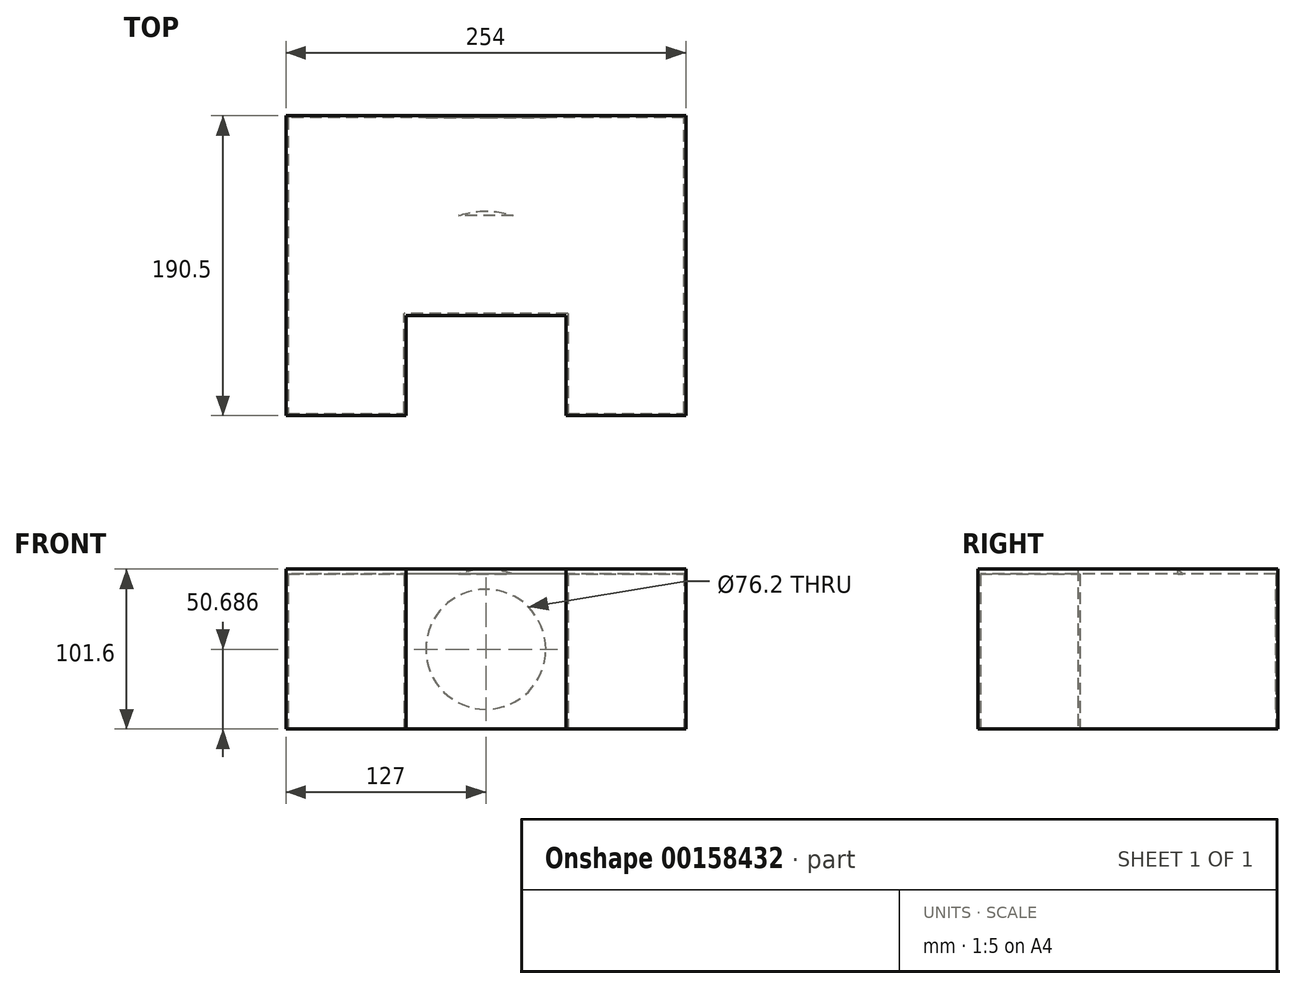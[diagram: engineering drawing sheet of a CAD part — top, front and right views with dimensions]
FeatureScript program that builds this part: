
annotation { "Feature Type Name" : "Feature", "Feature Type Description" : "" }
export const myFeature = defineFeature(function(context is Context, id is Id, definition is map)
    precondition{}
    {
        {
            var Q0;
            Q0=qCreatedBy(makeId("Top.planeOp"),FACE);
            var sketch = newSketch(context, id + "F0", { "sketchPlane" : qUnion([Q0])});
            skLineSegment(sketch, "E0.bottom", {"start": v(127, -63.5) * mm, "end": v(-127, -63.5) * mm});
            skLineSegment(sketch, "E0.top", {"start": v(127, 63.5) * mm, "end": v(-127, 63.5) * mm});
            skLineSegment(sketch, "E0.left", {"start": v(127, -63.5) * mm, "end": v(127, 63.5) * mm});
            skLineSegment(sketch, "E0.right", {"start": v(-127, -63.5) * mm, "end": v(-127, 63.5) * mm});
            skPoint(sketch, "E0.middle", {"position": v(0, 0) * mm});
            skLineSegment(sketch, "E1", {"start": v(-127, -63.5) * mm, "end": v(-50.8, -63.5) * mm});
            skLineSegment(sketch, "E2", {"start": v(127, -63.5) * mm, "end": v(50.8, -63.5) * mm});
            skLineSegment(sketch, "E3", {"start": v(-127, -63.5) * mm, "end": v(-127, -127) * mm});
            skLineSegment(sketch, "E4", {"start": v(127, -63.5) * mm, "end": v(127, -127) * mm});
            skLineSegment(sketch, "E5", {"start": v(-127, -127) * mm, "end": v(-50.8, -127) * mm});
            skLineSegment(sketch, "E6", {"start": v(127, -127) * mm, "end": v(50.8, -127) * mm});
            skLineSegment(sketch, "E7", {"start": v(-50.8, -63.5) * mm, "end": v(-50.8, -127) * mm});
            skLineSegment(sketch, "E8", {"start": v(50.8, -63.5) * mm, "end": v(50.8, -127) * mm});
            skSolve(sketch);
        }
        {
            var Q0;
            Q0 = qSketchRegion(id + "F0", true);
            extrude(context, id + "F1", {"entities" : qUnion([Q0]), "depth" : 101.6 * mm});
        }
        {
            var Q0;
            Q0=qCreatedBy(makeId("Top.planeOp"),FACE);
            var sketch = newSketch(context, id + "F2", { "sketchPlane" : qUnion([Q0])});
            skLineSegment(sketch, "E9.bottom", {"start": v(125.73, -62.23) * mm, "end": v(-125.73, -62.23) * mm});
            skLineSegment(sketch, "E9.top", {"start": v(125.73, 62.23) * mm, "end": v(-125.73, 62.23) * mm});
            skLineSegment(sketch, "E9.left", {"start": v(125.73, -62.23) * mm, "end": v(125.73, 62.23) * mm});
            skLineSegment(sketch, "E9.right", {"start": v(-125.73, -62.23) * mm, "end": v(-125.73, 62.23) * mm});
            skPoint(sketch, "E9.middle", {"position": v(0, 0) * mm});
            skLineSegment(sketch, "E10", {"start": v(-125.73, -62.23) * mm, "end": v(-125.73, -125.48) * mm});
            skLineSegment(sketch, "E11", {"start": v(-125.73, -125.48) * mm, "end": v(-52.07, -125.48) * mm});
            skLineSegment(sketch, "E12", {"start": v(-52.07, -125.48) * mm, "end": v(-52.07, -62.23) * mm});
            skLineSegment(sketch, "E13", {"start": v(-52.07, -62.23) * mm, "end": v(52.07, -62.23) * mm});
            skLineSegment(sketch, "E14", {"start": v(52.07, -62.23) * mm, "end": v(52.07, -125.48) * mm});
            skLineSegment(sketch, "E15", {"start": v(52.07, -125.48) * mm, "end": v(125.73, -125.48) * mm});
            skLineSegment(sketch, "E16", {"start": v(125.73, -125.48) * mm, "end": v(125.73, -62.23) * mm});
            skSolve(sketch);
        }
        {
            var Q0;
            Q0 = qSketchRegion(id + "F2", true);
            extrude(context, id + "F3", {"entities" : qUnion([Q0]), "operationType" : NewBodyOperationType.REMOVE, "depth" : 98.42 * mm});
        }
        {
            var Q0;
            Q0=qCreatedBy(makeId("Front.planeOp"),FACE);
            var sketch = newSketch(context, id + "F4", { "sketchPlane" : qUnion([Q0])});
            skCircle(sketch, "E17", {"center": v(0, 50.69) * mm, "radius": 50.33 * mm});
            skSolve(sketch);
        }
        {
            var Q0;
            Q0=sQuery(id+"F4.wireOp",VERTEX,"E17.center");
            var Q1;
            Q1=makeQuery(id+"F1.opExtrude","SWEPT_BODY",BODY,{"disambiguationData":[OSD([sQuery(id+"F0.wireOp",EDGE,"E0.bottom"),sQuery(id+"F0.wireOp",EDGE,"E0.top"),sQuery(id+"F0.wireOp",EDGE,"E0.left"),sQuery(id+"F0.wireOp",EDGE,"E0.right"),sQuery(id+"F0.wireOp",EDGE,"E3"),sQuery(id+"F0.wireOp",EDGE,"E4"),sQuery(id+"F0.wireOp",EDGE,"E5"),sQuery(id+"F0.wireOp",EDGE,"E6"),sQuery(id+"F0.wireOp",EDGE,"E7"),sQuery(id+"F0.wireOp",EDGE,"E8")])]});
            hole(context, id + "F5", {"style" : HoleStyle.C_SINK, "endStyle" : HoleEndStyle.THROUGH, "holeDiameter" : 76.2 * mm, "cSinkDiameter" : 101.6 * mm, "cSinkAngle" : 90 * degree, "startFromSketch" : true, "locations" : qUnion([Q0]), "scope" : qUnion([Q1]), "isTappedThrough" : true});
        }
    });
